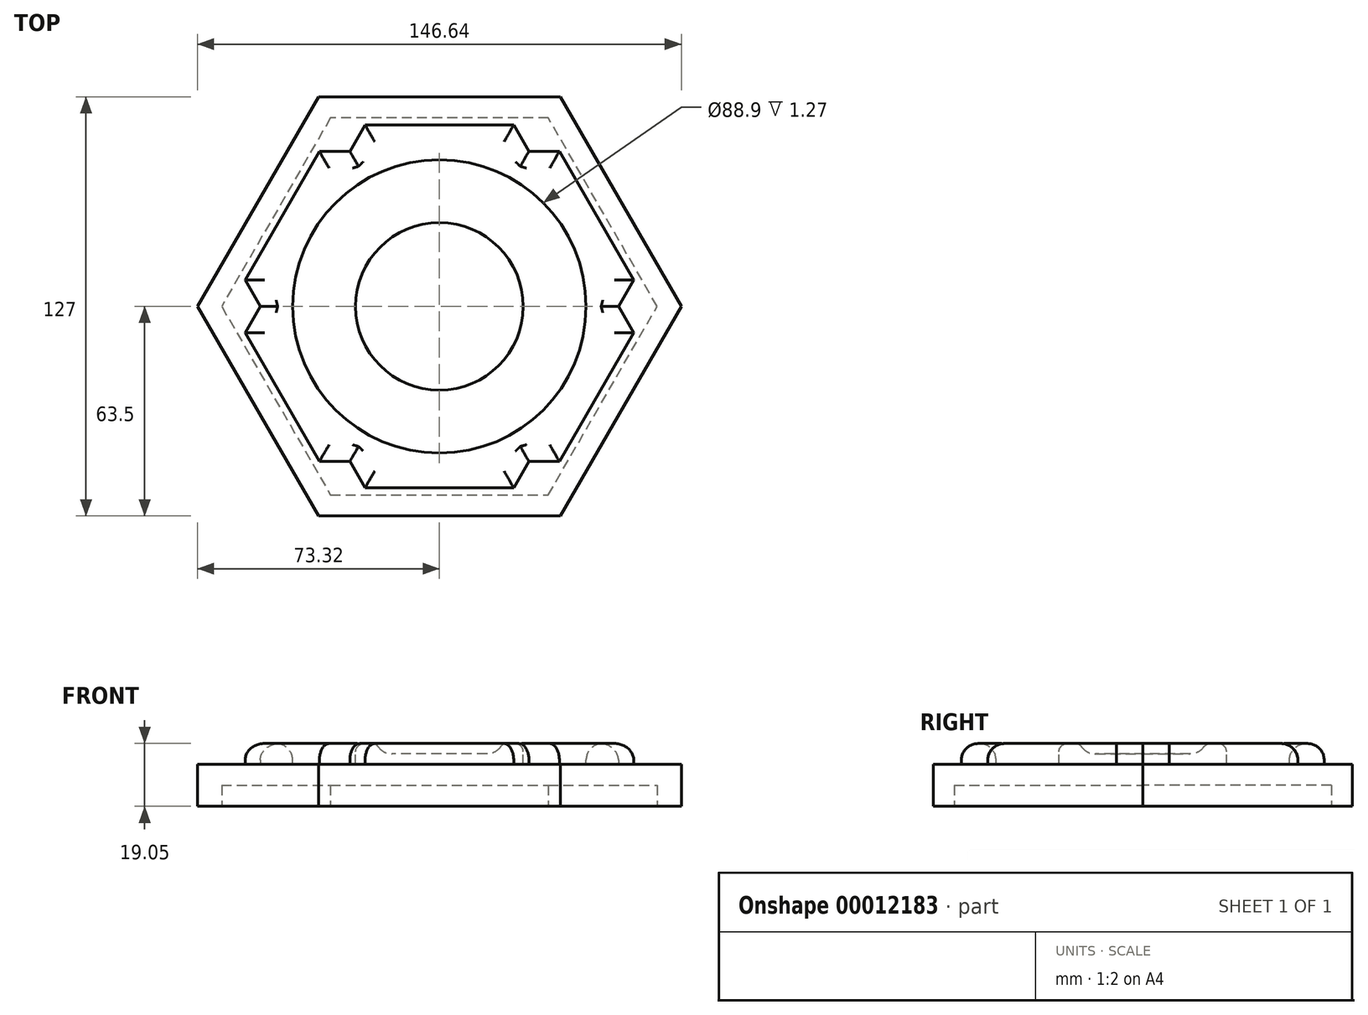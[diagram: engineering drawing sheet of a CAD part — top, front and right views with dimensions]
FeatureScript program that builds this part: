
annotation { "Feature Type Name" : "Feature", "Feature Type Description" : "" }
export const myFeature = defineFeature(function(context is Context, id is Id, definition is map)
    precondition{}
    {
        {
            var Q0;
            Q0=qCreatedBy(makeId("Top.planeOp"),FACE);
            var sketch = newSketch(context, id + "F0", { "sketchPlane" : qUnion([Q0])});
            skCircle(sketch, "E0.cCircle", {"center": v(0, 0) * mm, "radius": 63.5 * mm, "construction": true});
            skLineSegment(sketch, "E0.0", {"start": v(73.32, 0) * mm, "end": v(36.66, -63.5) * mm});
            skLineSegment(sketch, "E0.1", {"start": v(36.66, -63.5) * mm, "end": v(-36.66, -63.5) * mm});
            skLineSegment(sketch, "E0.2", {"start": v(-36.66, -63.5) * mm, "end": v(-73.32, 0) * mm});
            skLineSegment(sketch, "E0.3", {"start": v(-73.32, 0) * mm, "end": v(-36.66, 63.5) * mm});
            skLineSegment(sketch, "E0.4", {"start": v(-36.66, 63.5) * mm, "end": v(36.66, 63.5) * mm});
            skLineSegment(sketch, "E0.5", {"start": v(36.66, 63.5) * mm, "end": v(73.32, 0) * mm});
            skPoint(sketch, "E0.0.midPoint", {"position": v(55, -31.75) * mm});
            skCircle(sketch, "E1.cCircle", {"center": v(-36.66, 63.5) * mm, "radius": 19.05 * mm, "construction": true});
            skLineSegment(sketch, "E1.0", {"start": v(-27.14, 47) * mm, "end": v(-46.19, 47) * mm});
            skLineSegment(sketch, "E1.1", {"start": v(-46.19, 47) * mm, "end": v(-55.71, 63.5) * mm});
            skLineSegment(sketch, "E1.2", {"start": v(-55.71, 63.5) * mm, "end": v(-46.19, 80) * mm});
            skLineSegment(sketch, "E1.3", {"start": v(-46.19, 80) * mm, "end": v(-27.14, 80) * mm});
            skLineSegment(sketch, "E1.4", {"start": v(-27.14, 80) * mm, "end": v(-17.61, 63.5) * mm});
            skLineSegment(sketch, "E1.5", {"start": v(-17.61, 63.5) * mm, "end": v(-27.14, 47) * mm});
            skCircle(sketch, "E2.cCircle", {"center": v(-73.32, 0) * mm, "radius": 19.05 * mm, "construction": true});
            skLineSegment(sketch, "E2.0", {"start": v(-54.27, 0) * mm, "end": v(-63.8, -16.5) * mm});
            skLineSegment(sketch, "E2.1", {"start": v(-63.8, -16.5) * mm, "end": v(-82.85, -16.5) * mm});
            skLineSegment(sketch, "E2.2", {"start": v(-82.85, -16.5) * mm, "end": v(-92.37, 0) * mm});
            skLineSegment(sketch, "E2.3", {"start": v(-92.37, 0) * mm, "end": v(-82.85, 16.5) * mm});
            skLineSegment(sketch, "E2.4", {"start": v(-82.85, 16.5) * mm, "end": v(-63.8, 16.5) * mm});
            skLineSegment(sketch, "E2.5", {"start": v(-63.8, 16.5) * mm, "end": v(-54.27, 0) * mm});
            skCircle(sketch, "E3.cCircle", {"center": v(-36.66, -63.5) * mm, "radius": 19.05 * mm, "construction": true});
            skLineSegment(sketch, "E3.0", {"start": v(-17.61, -63.5) * mm, "end": v(-27.14, -80) * mm});
            skLineSegment(sketch, "E3.1", {"start": v(-27.14, -80) * mm, "end": v(-46.19, -80) * mm});
            skLineSegment(sketch, "E3.2", {"start": v(-46.19, -80) * mm, "end": v(-55.71, -63.5) * mm});
            skLineSegment(sketch, "E3.3", {"start": v(-55.71, -63.5) * mm, "end": v(-46.19, -47) * mm});
            skLineSegment(sketch, "E3.4", {"start": v(-46.19, -47) * mm, "end": v(-27.14, -47) * mm});
            skLineSegment(sketch, "E3.5", {"start": v(-27.14, -47) * mm, "end": v(-17.61, -63.5) * mm});
            skCircle(sketch, "E4.cCircle", {"center": v(36.66, -63.5) * mm, "radius": 19.05 * mm, "construction": true});
            skLineSegment(sketch, "E4.0", {"start": v(17.61, -63.5) * mm, "end": v(27.14, -47) * mm});
            skLineSegment(sketch, "E4.1", {"start": v(27.14, -47) * mm, "end": v(46.19, -47) * mm});
            skLineSegment(sketch, "E4.2", {"start": v(46.19, -47) * mm, "end": v(55.71, -63.5) * mm});
            skLineSegment(sketch, "E4.3", {"start": v(55.71, -63.5) * mm, "end": v(46.19, -80) * mm});
            skLineSegment(sketch, "E4.4", {"start": v(46.19, -80) * mm, "end": v(27.14, -80) * mm});
            skLineSegment(sketch, "E4.5", {"start": v(27.14, -80) * mm, "end": v(17.61, -63.5) * mm});
            skCircle(sketch, "E5.cCircle", {"center": v(73.32, 0) * mm, "radius": 19.05 * mm, "construction": true});
            skLineSegment(sketch, "E5.0", {"start": v(54.27, 0) * mm, "end": v(63.8, 16.5) * mm});
            skLineSegment(sketch, "E5.1", {"start": v(63.8, 16.5) * mm, "end": v(82.85, 16.5) * mm});
            skLineSegment(sketch, "E5.2", {"start": v(82.85, 16.5) * mm, "end": v(92.37, 0) * mm});
            skLineSegment(sketch, "E5.3", {"start": v(92.37, 0) * mm, "end": v(82.85, -16.5) * mm});
            skLineSegment(sketch, "E5.4", {"start": v(82.85, -16.5) * mm, "end": v(63.8, -16.5) * mm});
            skLineSegment(sketch, "E5.5", {"start": v(63.8, -16.5) * mm, "end": v(54.27, 0) * mm});
            skCircle(sketch, "E6.cCircle", {"center": v(36.66, 63.5) * mm, "radius": 19.05 * mm, "construction": true});
            skLineSegment(sketch, "E6.0", {"start": v(17.61, 63.5) * mm, "end": v(27.14, 80) * mm});
            skLineSegment(sketch, "E6.1", {"start": v(27.14, 80) * mm, "end": v(46.19, 80) * mm});
            skLineSegment(sketch, "E6.2", {"start": v(46.19, 80) * mm, "end": v(55.71, 63.5) * mm});
            skLineSegment(sketch, "E6.3", {"start": v(55.71, 63.5) * mm, "end": v(46.19, 47) * mm});
            skLineSegment(sketch, "E6.4", {"start": v(46.19, 47) * mm, "end": v(27.14, 47) * mm});
            skLineSegment(sketch, "E6.5", {"start": v(27.14, 47) * mm, "end": v(17.61, 63.5) * mm});
            skLineSegment(sketch, "E7.0", {"start": v(63.5, 0) * mm, "end": v(31.75, -55) * mm});
            skLineSegment(sketch, "E7.1", {"start": v(31.75, -55) * mm, "end": v(-31.75, -55) * mm});
            skLineSegment(sketch, "E7.2", {"start": v(-31.75, -55) * mm, "end": v(-63.5, 0) * mm});
            skLineSegment(sketch, "E7.3", {"start": v(-63.5, 0) * mm, "end": v(-31.75, 55) * mm});
            skLineSegment(sketch, "E7.4", {"start": v(-31.75, 55) * mm, "end": v(31.75, 55) * mm});
            skLineSegment(sketch, "E7.5", {"start": v(31.75, 55) * mm, "end": v(63.5, 0) * mm});
            skSolve(sketch);
        }
        {
            var Q0;
            {var subQ8=sQuery(id+"F0.wireOp",EDGE,"E1.5");var subQ13=sQuery(id+"F0.wireOp",EDGE,"E1.0");var subQ35=makeQuery(id+"F0.imprint","INTERSECT",VERTEX,{"derivedFrom":[subQ13,subQ8]});Q0=makeQuery(id+"F0.imprint","IMPRINT",FACE,{"disambiguationData":[TD([[makeQuery(id+"F0.imprint","IMPRINT",EDGE,{"disambiguationData":[TD([[subQ35,-1.0]])],"derivedFrom":subQ13}),1.0]])]});}
            extrude(context, id + "F1", {"entities" : qUnion([Q0]), "depth" : 6.35 * mm});
        }
        {
            var Q0;
            {var subQ1=sQuery(id+"F0.wireOp",EDGE,"E1.5");var subQ5=sQuery(id+"F0.wireOp",EDGE,"E1.0");var subQ7=makeQuery(id+"F0.imprint","INTERSECT",VERTEX,{"derivedFrom":[subQ5,subQ1]});Q0=makeQuery(id+"F0.imprint","IMPRINT",FACE,{"disambiguationData":[TD([[makeQuery(id+"F0.imprint","IMPRINT",EDGE,{"disambiguationData":[TD([[subQ7,-1.0]])],"derivedFrom":subQ5}),-1.0]])]});}
            var Q1;
            {var subQ0=sQuery(id+"F0.wireOp",EDGE,"E7.4");var subQ3=sQuery(id+"F0.wireOp",EDGE,"E7.3");var subQ4=makeQuery(id+"F0.imprint","INTERSECT",VERTEX,{"derivedFrom":[subQ3,subQ0]});Q1=makeQuery(id+"F0.imprint","IMPRINT",FACE,{"disambiguationData":[TD([[makeQuery(id+"F0.imprint","IMPRINT",EDGE,{"disambiguationData":[TD([[subQ4,1.0]])],"derivedFrom":subQ3}),1.0]])]});}
            var Q2;
            {var subQ0=sQuery(id+"F0.wireOp",EDGE,"E7.3");var subQ3=sQuery(id+"F0.wireOp",EDGE,"E1.0");var subQ4=makeQuery(id+"F0.imprint","INTERSECT",VERTEX,{"derivedFrom":[subQ3,subQ0]});Q2=makeQuery(id+"F0.imprint","IMPRINT",FACE,{"disambiguationData":[TD([[makeQuery(id+"F0.imprint","IMPRINT",EDGE,{"disambiguationData":[TD([[subQ4,1.0]])],"derivedFrom":subQ0}),1.0]])]});}
            var Q3;
            {var subQ1=sQuery(id+"F0.wireOp",EDGE,"E7.3");var subQ6=sQuery(id+"F0.wireOp",EDGE,"E7.2");var subQ10=makeQuery(id+"F0.imprint","INTERSECT",VERTEX,{"derivedFrom":[subQ6,subQ1]});Q3=makeQuery(id+"F0.imprint","IMPRINT",FACE,{"disambiguationData":[TD([[makeQuery(id+"F0.imprint","IMPRINT",EDGE,{"disambiguationData":[TD([[subQ10,1.0]])],"derivedFrom":subQ6}),1.0]])]});}
            var Q4;
            {var subQ1=sQuery(id+"F0.wireOp",EDGE,"E2.5");var subQ5=sQuery(id+"F0.wireOp",EDGE,"E2.0");var subQ7=makeQuery(id+"F0.imprint","INTERSECT",VERTEX,{"derivedFrom":[subQ5,subQ1]});Q4=makeQuery(id+"F0.imprint","IMPRINT",FACE,{"disambiguationData":[TD([[makeQuery(id+"F0.imprint","IMPRINT",EDGE,{"disambiguationData":[TD([[subQ7,-1.0]])],"derivedFrom":subQ5}),-1.0]])]});}
            var Q5;
            {var subQ0=sQuery(id+"F0.wireOp",EDGE,"E7.2");var subQ3=sQuery(id+"F0.wireOp",EDGE,"E2.0");var subQ4=makeQuery(id+"F0.imprint","INTERSECT",VERTEX,{"derivedFrom":[subQ3,subQ0]});Q5=makeQuery(id+"F0.imprint","IMPRINT",FACE,{"disambiguationData":[TD([[makeQuery(id+"F0.imprint","IMPRINT",EDGE,{"disambiguationData":[TD([[subQ4,1.0]])],"derivedFrom":subQ0}),1.0]])]});}
            var Q6;
            {var subQ0=sQuery(id+"F0.wireOp",EDGE,"E7.2");var subQ3=sQuery(id+"F0.wireOp",EDGE,"E7.1");var subQ4=makeQuery(id+"F0.imprint","INTERSECT",VERTEX,{"derivedFrom":[subQ3,subQ0]});Q6=makeQuery(id+"F0.imprint","IMPRINT",FACE,{"disambiguationData":[TD([[makeQuery(id+"F0.imprint","IMPRINT",EDGE,{"disambiguationData":[TD([[subQ4,1.0]])],"derivedFrom":subQ3}),1.0]])]});}
            var Q7;
            {var subQ1=sQuery(id+"F0.wireOp",EDGE,"E3.4");var subQ5=sQuery(id+"F0.wireOp",EDGE,"E3.5");var subQ7=makeQuery(id+"F0.imprint","INTERSECT",VERTEX,{"derivedFrom":[subQ1,subQ5]});Q7=makeQuery(id+"F0.imprint","IMPRINT",FACE,{"disambiguationData":[TD([[makeQuery(id+"F0.imprint","IMPRINT",EDGE,{"disambiguationData":[TD([[subQ7,1.0]])],"derivedFrom":subQ1}),-1.0]])]});}
            var Q8;
            {var subQ0=sQuery(id+"F0.wireOp",EDGE,"E7.1");var subQ3=sQuery(id+"F0.wireOp",EDGE,"E3.5");var subQ4=makeQuery(id+"F0.imprint","INTERSECT",VERTEX,{"derivedFrom":[subQ3,subQ0]});Q8=makeQuery(id+"F0.imprint","IMPRINT",FACE,{"disambiguationData":[TD([[makeQuery(id+"F0.imprint","IMPRINT",EDGE,{"disambiguationData":[TD([[subQ4,1.0]])],"derivedFrom":subQ0}),1.0]])]});}
            var Q9;
            {var subQ0=sQuery(id+"F0.wireOp",EDGE,"E7.1");var subQ3=sQuery(id+"F0.wireOp",EDGE,"E7.0");var subQ4=makeQuery(id+"F0.imprint","INTERSECT",VERTEX,{"derivedFrom":[subQ3,subQ0]});Q9=makeQuery(id+"F0.imprint","IMPRINT",FACE,{"disambiguationData":[TD([[makeQuery(id+"F0.imprint","IMPRINT",EDGE,{"disambiguationData":[TD([[subQ4,1.0]])],"derivedFrom":subQ3}),1.0]])]});}
            var Q10;
            {var subQ1=sQuery(id+"F0.wireOp",EDGE,"E4.0");var subQ5=sQuery(id+"F0.wireOp",EDGE,"E4.1");var subQ7=makeQuery(id+"F0.imprint","INTERSECT",VERTEX,{"derivedFrom":[subQ1,subQ5]});Q10=makeQuery(id+"F0.imprint","IMPRINT",FACE,{"disambiguationData":[TD([[makeQuery(id+"F0.imprint","IMPRINT",EDGE,{"disambiguationData":[TD([[subQ7,1.0]])],"derivedFrom":subQ1}),-1.0]])]});}
            var Q11;
            {var subQ1=sQuery(id+"F0.wireOp",EDGE,"E7.0");var subQ5=sQuery(id+"F0.wireOp",EDGE,"E4.1");var subQ6=makeQuery(id+"F0.imprint","INTERSECT",VERTEX,{"derivedFrom":[subQ5,subQ1]});Q11=makeQuery(id+"F0.imprint","IMPRINT",FACE,{"disambiguationData":[TD([[makeQuery(id+"F0.imprint","IMPRINT",EDGE,{"disambiguationData":[TD([[subQ6,1.0]])],"derivedFrom":subQ1}),1.0]])]});}
            var Q12;
            {var subQ0=sQuery(id+"F0.wireOp",EDGE,"E7.5");var subQ3=sQuery(id+"F0.wireOp",EDGE,"E7.0");var subQ4=makeQuery(id+"F0.imprint","INTERSECT",VERTEX,{"derivedFrom":[subQ3,subQ0]});Q12=makeQuery(id+"F0.imprint","IMPRINT",FACE,{"disambiguationData":[TD([[makeQuery(id+"F0.imprint","IMPRINT",EDGE,{"disambiguationData":[TD([[subQ4,-1.0]])],"derivedFrom":subQ3}),1.0]])]});}
            var Q13;
            {var subQ1=sQuery(id+"F0.wireOp",EDGE,"E5.0");var subQ5=sQuery(id+"F0.wireOp",EDGE,"E5.5");var subQ7=makeQuery(id+"F0.imprint","INTERSECT",VERTEX,{"derivedFrom":[subQ1,subQ5]});Q13=makeQuery(id+"F0.imprint","IMPRINT",FACE,{"disambiguationData":[TD([[makeQuery(id+"F0.imprint","IMPRINT",EDGE,{"disambiguationData":[TD([[subQ7,-1.0]])],"derivedFrom":subQ1}),-1.0]])]});}
            var Q14;
            {var subQ1=sQuery(id+"F0.wireOp",EDGE,"E7.5");var subQ5=sQuery(id+"F0.wireOp",EDGE,"E5.0");var subQ6=makeQuery(id+"F0.imprint","INTERSECT",VERTEX,{"derivedFrom":[subQ5,subQ1]});Q14=makeQuery(id+"F0.imprint","IMPRINT",FACE,{"disambiguationData":[TD([[makeQuery(id+"F0.imprint","IMPRINT",EDGE,{"disambiguationData":[TD([[subQ6,1.0]])],"derivedFrom":subQ1}),1.0]])]});}
            var Q15;
            {var subQ1=sQuery(id+"F0.wireOp",EDGE,"E6.5");var subQ5=sQuery(id+"F0.wireOp",EDGE,"E6.4");var subQ6=makeQuery(id+"F0.imprint","INTERSECT",VERTEX,{"derivedFrom":[subQ5,subQ1]});Q15=makeQuery(id+"F0.imprint","IMPRINT",FACE,{"disambiguationData":[TD([[makeQuery(id+"F0.imprint","IMPRINT",EDGE,{"disambiguationData":[TD([[subQ6,1.0]])],"derivedFrom":subQ5}),-1.0]])]});}
            var Q16;
            {var subQ1=sQuery(id+"F0.wireOp",EDGE,"E7.4");var subQ5=sQuery(id+"F0.wireOp",EDGE,"E7.5");var subQ8=makeQuery(id+"F0.imprint","INTERSECT",VERTEX,{"derivedFrom":[subQ1,subQ5]});Q16=makeQuery(id+"F0.imprint","IMPRINT",FACE,{"disambiguationData":[TD([[makeQuery(id+"F0.imprint","IMPRINT",EDGE,{"disambiguationData":[TD([[subQ8,1.0]])],"derivedFrom":subQ1}),1.0]])]});}
            var Q17;
            {var subQ1=sQuery(id+"F0.wireOp",EDGE,"E7.4");var subQ5=sQuery(id+"F0.wireOp",EDGE,"E1.5");var subQ6=makeQuery(id+"F0.imprint","INTERSECT",VERTEX,{"derivedFrom":[subQ5,subQ1]});Q17=makeQuery(id+"F0.imprint","IMPRINT",FACE,{"disambiguationData":[TD([[makeQuery(id+"F0.imprint","IMPRINT",EDGE,{"disambiguationData":[TD([[subQ6,-1.0]])],"derivedFrom":subQ1}),1.0]])]});}
            var Q18;
            Q18=makeQuery(id+"F1.opExtrude","CAP_FACE",FACE,{"disambiguationData":[OSD([sQuery(id+"F0.wireOp",EDGE,"E1.0"),sQuery(id+"F0.wireOp",EDGE,"E1.5"),sQuery(id+"F0.wireOp",EDGE,"E2.0"),sQuery(id+"F0.wireOp",EDGE,"E2.5"),sQuery(id+"F0.wireOp",EDGE,"E3.4"),sQuery(id+"F0.wireOp",EDGE,"E3.5"),sQuery(id+"F0.wireOp",EDGE,"E4.0"),sQuery(id+"F0.wireOp",EDGE,"E4.1"),sQuery(id+"F0.wireOp",EDGE,"E5.0"),sQuery(id+"F0.wireOp",EDGE,"E5.5"),sQuery(id+"F0.wireOp",EDGE,"E6.4"),sQuery(id+"F0.wireOp",EDGE,"E6.5"),sQuery(id+"F0.wireOp",EDGE,"E7.0"),sQuery(id+"F0.wireOp",EDGE,"E7.1"),sQuery(id+"F0.wireOp",EDGE,"E7.2"),sQuery(id+"F0.wireOp",EDGE,"E7.3"),sQuery(id+"F0.wireOp",EDGE,"E7.4"),sQuery(id+"F0.wireOp",EDGE,"E7.5")])],"isStart":false});
            extrude(context, id + "F2", {"entities" : qUnion([Q0, Q1, Q2, Q3, Q4, Q5, Q6, Q7, Q8, Q9, Q10, Q11, Q12, Q13, Q14, Q15, Q16, Q17, Q18]), "operationType" : NewBodyOperationType.ADD, "depth" : 12.7 * mm});
        }
        {
            var Q0;
            Q0=makeQuery(id+"F2.opExtrude","CAP_FACE",FACE,{"disambiguationData":[OSD([sQuery(id+"F0.wireOp",EDGE,"E1.0"),sQuery(id+"F0.wireOp",EDGE,"E1.5"),sQuery(id+"F0.wireOp",EDGE,"E2.0"),sQuery(id+"F0.wireOp",EDGE,"E2.5"),sQuery(id+"F0.wireOp",EDGE,"E3.4"),sQuery(id+"F0.wireOp",EDGE,"E3.5"),sQuery(id+"F0.wireOp",EDGE,"E4.0"),sQuery(id+"F0.wireOp",EDGE,"E4.1"),sQuery(id+"F0.wireOp",EDGE,"E5.0"),sQuery(id+"F0.wireOp",EDGE,"E5.5"),sQuery(id+"F0.wireOp",EDGE,"E6.4"),sQuery(id+"F0.wireOp",EDGE,"E6.5"),sQuery(id+"F0.wireOp",EDGE,"E7.0"),sQuery(id+"F0.wireOp",EDGE,"E7.1"),sQuery(id+"F0.wireOp",EDGE,"E7.2"),sQuery(id+"F0.wireOp",EDGE,"E7.3"),sQuery(id+"F0.wireOp",EDGE,"E7.4"),sQuery(id+"F0.wireOp",EDGE,"E7.5")])],"isStart":false});
            var sketch = newSketch(context, id + "F3", { "sketchPlane" : qUnion([Q0])});
            skCircle(sketch, "E8", {"center": v(0, 0) * mm, "radius": 19.05 * mm});
            skSolve(sketch);
        }
        {
            var Q0;
            Q0=makeQuery(id+"F3.imprint","IMPRINT",FACE,{"disambiguationData":[TD([[makeQuery(id+"F3.imprint","IMPRINT",EDGE,{"derivedFrom":sQuery(id+"F3.wireOp",EDGE,"E8")}),1.0]])]});
            extrude(context, id + "F4", {"entities" : qUnion([Q0]), "operationType" : NewBodyOperationType.REMOVE, "endBound" : BoundingType.SYMMETRIC, "oppositeDirection" : true, "depth" : 6.35 * mm});
        }
        {
            var Q0;
            Q0=makeQuery(id+"F4.boolean.opBoolean","COPY",EDGE,{"derivedFrom":makeQuery(id+"F4.opExtrude","CAP_EDGE",EDGE,{"disambiguationData":[OSD([sQuery(id+"F3.wireOp",EDGE,"E8")])],"isStart":false})});
            fillet(context, id + "F5", {"entities" : qUnion([Q0]), "radius" : 5.08 * mm, "tangentPropagation" : true, "allowEdgeOverflow" : false});
        }
        {
            var Q0;
            Q0=makeQuery(id+"F2.opExtrude","CAP_FACE",FACE,{"disambiguationData":[OSD([sQuery(id+"F0.wireOp",EDGE,"E1.0"),sQuery(id+"F0.wireOp",EDGE,"E1.5"),sQuery(id+"F0.wireOp",EDGE,"E2.0"),sQuery(id+"F0.wireOp",EDGE,"E2.5"),sQuery(id+"F0.wireOp",EDGE,"E3.4"),sQuery(id+"F0.wireOp",EDGE,"E3.5"),sQuery(id+"F0.wireOp",EDGE,"E4.0"),sQuery(id+"F0.wireOp",EDGE,"E4.1"),sQuery(id+"F0.wireOp",EDGE,"E5.0"),sQuery(id+"F0.wireOp",EDGE,"E5.5"),sQuery(id+"F0.wireOp",EDGE,"E6.4"),sQuery(id+"F0.wireOp",EDGE,"E6.5"),sQuery(id+"F0.wireOp",EDGE,"E7.0"),sQuery(id+"F0.wireOp",EDGE,"E7.1"),sQuery(id+"F0.wireOp",EDGE,"E7.2"),sQuery(id+"F0.wireOp",EDGE,"E7.3"),sQuery(id+"F0.wireOp",EDGE,"E7.4"),sQuery(id+"F0.wireOp",EDGE,"E7.5")])],"isStart":false});
            var sketch = newSketch(context, id + "F6", { "sketchPlane" : qUnion([Q0])});
            skCircle(sketch, "E9", {"center": v(0, 0) * mm, "radius": 44.45 * mm});
            skCircle(sketch, "E10", {"center": v(0, 0) * mm, "radius": 25.4 * mm});
            skSolve(sketch);
        }
        {
            var Q0;
            Q0=makeQuery(id+"F6.imprint","IMPRINT",FACE,{"disambiguationData":[TD([[makeQuery(id+"F6.imprint","IMPRINT",EDGE,{"derivedFrom":sQuery(id+"F6.wireOp",EDGE,"E9")}),1.0]])]});
            extrude(context, id + "F7", {"entities" : qUnion([Q0]), "operationType" : NewBodyOperationType.REMOVE, "oppositeDirection" : true, "depth" : 6.35 * mm});
        }
        {
            var Q0;
            {var subQ0=sQuery(id+"F0.wireOp",EDGE,"E1.0");var subQ1=sQuery(id+"F0.wireOp",EDGE,"E1.5");var subQ2=sQuery(id+"F0.wireOp",EDGE,"E2.0");var subQ3=sQuery(id+"F0.wireOp",EDGE,"E2.5");var subQ4=sQuery(id+"F0.wireOp",EDGE,"E3.4");var subQ5=sQuery(id+"F0.wireOp",EDGE,"E3.5");var subQ6=sQuery(id+"F0.wireOp",EDGE,"E4.0");var subQ7=sQuery(id+"F0.wireOp",EDGE,"E4.1");var subQ8=sQuery(id+"F0.wireOp",EDGE,"E5.0");var subQ9=sQuery(id+"F0.wireOp",EDGE,"E5.5");var subQ10=sQuery(id+"F0.wireOp",EDGE,"E6.4");var subQ11=sQuery(id+"F0.wireOp",EDGE,"E6.5");var subQ12=sQuery(id+"F0.wireOp",EDGE,"E7.0");var subQ13=sQuery(id+"F0.wireOp",EDGE,"E7.1");var subQ14=sQuery(id+"F0.wireOp",EDGE,"E7.2");var subQ15=sQuery(id+"F0.wireOp",EDGE,"E7.3");var subQ16=sQuery(id+"F0.wireOp",EDGE,"E7.4");var subQ17=sQuery(id+"F0.wireOp",EDGE,"E7.5");Q0=makeQuery(id+"F2.boolean.opBoolean","MERGE",FACE,{"derivedFrom":[makeQuery(id+"F1.opExtrude","CAP_FACE",FACE,{"disambiguationData":[OSD([subQ0,subQ1,subQ2,subQ3,subQ4,subQ5,subQ6,subQ7,subQ8,subQ9,subQ10,subQ11,subQ12,subQ13,subQ14,subQ15,subQ16,subQ17])],"isStart":true}),makeQuery(id+"F2.opExtrude","CAP_FACE",FACE,{"disambiguationData":[OSD([sQuery(id+"F0.wireOp",EDGE,"E0.0"),sQuery(id+"F0.wireOp",EDGE,"E0.1"),sQuery(id+"F0.wireOp",EDGE,"E0.2"),sQuery(id+"F0.wireOp",EDGE,"E0.3"),sQuery(id+"F0.wireOp",EDGE,"E0.4"),sQuery(id+"F0.wireOp",EDGE,"E0.5"),subQ0,subQ1,subQ2,subQ3,subQ4,subQ5,subQ6,subQ7,subQ8,subQ9,subQ10,subQ11,subQ12,subQ13,subQ14,subQ15,subQ16,subQ17])],"isStart":true})]});}
            var sketch = newSketch(context, id + "F8", { "sketchPlane" : qUnion([Q0])});
            skSolve(sketch);
        }
        {
            var Q0;
            {var subQ0=sQuery(id+"F0.wireOp",EDGE,"E1.0");var subQ1=sQuery(id+"F0.wireOp",EDGE,"E1.5");var subQ2=sQuery(id+"F0.wireOp",EDGE,"E2.0");var subQ3=sQuery(id+"F0.wireOp",EDGE,"E2.5");var subQ4=sQuery(id+"F0.wireOp",EDGE,"E3.4");var subQ5=sQuery(id+"F0.wireOp",EDGE,"E3.5");var subQ6=sQuery(id+"F0.wireOp",EDGE,"E4.0");var subQ7=sQuery(id+"F0.wireOp",EDGE,"E4.1");var subQ8=sQuery(id+"F0.wireOp",EDGE,"E5.0");var subQ9=sQuery(id+"F0.wireOp",EDGE,"E5.5");var subQ10=sQuery(id+"F0.wireOp",EDGE,"E6.4");var subQ11=sQuery(id+"F0.wireOp",EDGE,"E6.5");var subQ12=sQuery(id+"F0.wireOp",EDGE,"E7.0");var subQ13=sQuery(id+"F0.wireOp",EDGE,"E7.1");var subQ14=sQuery(id+"F0.wireOp",EDGE,"E7.2");var subQ15=sQuery(id+"F0.wireOp",EDGE,"E7.3");var subQ16=sQuery(id+"F0.wireOp",EDGE,"E7.4");var subQ17=sQuery(id+"F0.wireOp",EDGE,"E7.5");Q0=makeQuery(id+"F7.boolean.opBoolean","SPLIT",FACE,{"disambiguationData":[TD([makeQuery(id+"F7.opExtrude","SWEPT_FACE",FACE,{"disambiguationData":[OSD([sQuery(id+"F6.wireOp",EDGE,"E9")])]})])],"derivedFrom":makeQuery(id+"F2.opExtrude","CAP_FACE",FACE,{"disambiguationData":[OSD([subQ0,subQ1,subQ2,subQ3,subQ4,subQ5,subQ6,subQ7,subQ8,subQ9,subQ10,subQ11,subQ12,subQ13,subQ14,subQ15,subQ16,subQ17])],"isStart":false})});}
            fillet(context, id + "F9", {"entities" : qUnion([Q0]), "radius" : 5.08 * mm, "tangentPropagation" : true, "allowEdgeOverflow" : false});
        }
        {
            var Q0;
            Q0=makeQuery(id+"F7.boolean.opBoolean","SPLIT",FACE,{"disambiguationData":[TD([makeQuery(id+"F5.opFillet","BLEND_FACE",FACE,{"disambiguationData":[OSD([sQuery(id+"F3.wireOp",EDGE,"E8")])]})])],"derivedFrom":makeQuery(id+"F2.opExtrude","CAP_FACE",FACE,{"disambiguationData":[OSD([sQuery(id+"F0.wireOp",EDGE,"E1.0"),sQuery(id+"F0.wireOp",EDGE,"E1.5"),sQuery(id+"F0.wireOp",EDGE,"E2.0"),sQuery(id+"F0.wireOp",EDGE,"E2.5"),sQuery(id+"F0.wireOp",EDGE,"E3.4"),sQuery(id+"F0.wireOp",EDGE,"E3.5"),sQuery(id+"F0.wireOp",EDGE,"E4.0"),sQuery(id+"F0.wireOp",EDGE,"E4.1"),sQuery(id+"F0.wireOp",EDGE,"E5.0"),sQuery(id+"F0.wireOp",EDGE,"E5.5"),sQuery(id+"F0.wireOp",EDGE,"E6.4"),sQuery(id+"F0.wireOp",EDGE,"E6.5"),sQuery(id+"F0.wireOp",EDGE,"E7.0"),sQuery(id+"F0.wireOp",EDGE,"E7.1"),sQuery(id+"F0.wireOp",EDGE,"E7.2"),sQuery(id+"F0.wireOp",EDGE,"E7.3"),sQuery(id+"F0.wireOp",EDGE,"E7.4"),sQuery(id+"F0.wireOp",EDGE,"E7.5")])],"isStart":false})});
            fillet(context, id + "F10", {"entities" : qUnion([Q0]), "radius" : 2.54 * mm, "tangentPropagation" : true, "allowEdgeOverflow" : false});
        }
        {
            var Q0;
            Q0=makeQuery(id+"F8.imprint","IMPRINT",FACE,{"disambiguationData":[TD([[makeQuery(id+"F8.imprint","IMPRINT",EDGE,{"derivedFrom":makeQuery(id+"F2.opExtrude","CAP_EDGE",EDGE,{"disambiguationData":[OSD([sQuery(id+"F0.wireOp",EDGE,"E0.0")])],"isStart":true})}),1.0]])]});
            var sketch = newSketch(context, id + "F11", { "sketchPlane" : qUnion([Q0])});
            skCircle(sketch, "E11.cCircle", {"center": v(0, 0) * mm, "radius": 57.15 * mm, "construction": true});
            skLineSegment(sketch, "E11.0", {"start": v(33, 57.15) * mm, "end": v(66, 0) * mm});
            skLineSegment(sketch, "E11.1", {"start": v(66, 0) * mm, "end": v(33, -57.15) * mm});
            skLineSegment(sketch, "E11.2", {"start": v(33, -57.15) * mm, "end": v(-33, -57.15) * mm});
            skLineSegment(sketch, "E11.3", {"start": v(-33, -57.15) * mm, "end": v(-66, 0) * mm});
            skLineSegment(sketch, "E11.4", {"start": v(-66, 0) * mm, "end": v(-33, 57.15) * mm});
            skLineSegment(sketch, "E11.5", {"start": v(-33, 57.15) * mm, "end": v(33, 57.15) * mm});
            skPoint(sketch, "E11.0.midPoint", {"position": v(49.5, 28.57) * mm});
            skSolve(sketch);
        }
        {
            var Q0;
            Q0=makeQuery(id+"F11.imprint","IMPRINT",FACE,{"disambiguationData":[TD([[makeQuery(id+"F11.imprint","IMPRINT",EDGE,{"derivedFrom":sQuery(id+"F11.wireOp",EDGE,"E11.0")}),-1.0]])]});
            extrude(context, id + "F12", {"entities" : qUnion([Q0]), "operationType" : NewBodyOperationType.REMOVE, "oppositeDirection" : true, "depth" : 6.35 * mm});
        }
    });
